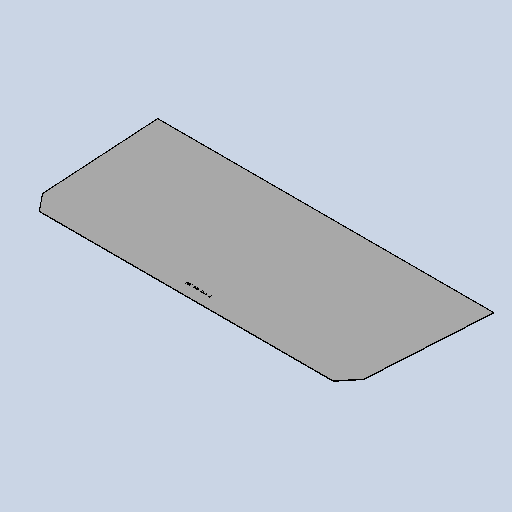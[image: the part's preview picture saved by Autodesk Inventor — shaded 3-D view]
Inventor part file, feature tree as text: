
AUTODESK INVENTOR PART (.ipt)
format: ipt  version: 2025 (Build 290162010, 162A)  size: 188,928 bytes
history: native  units: mm
features: other x6, sketch x2, reference x2, sheet_metal_op x1, mirror x1
ambient origin geometry x8: Origin, YZ Plane, XZ Plane, XY Plane, X Axis, Y Axis, Z Axis, Center Point
bodies: Solid1 (feature_tree)
feature tree (12):
  sheet_metal_op  "Face1"
  mirror  "Mirror1"
  other  "Mark1"
  sketch  "Sketch1"  dims[d2=2.0mm]
  other  "Plate1"
  reference  "Reference3"
  reference  "Reference5"
  sketch  "Sketch2"  dims[d3=10.0mm d4=10.0mm d5=10.0mm d6=12.0mm d7=110.0mm d8=50.0mm]
  other  "ASY MSC 001 отстойник осветлитель.iam"
  other  "ASY MSC 202 LEFT BOARD:1"
  other  "MSC 027 sheet board face 1.ipt:1"
  other  "Definition1"
